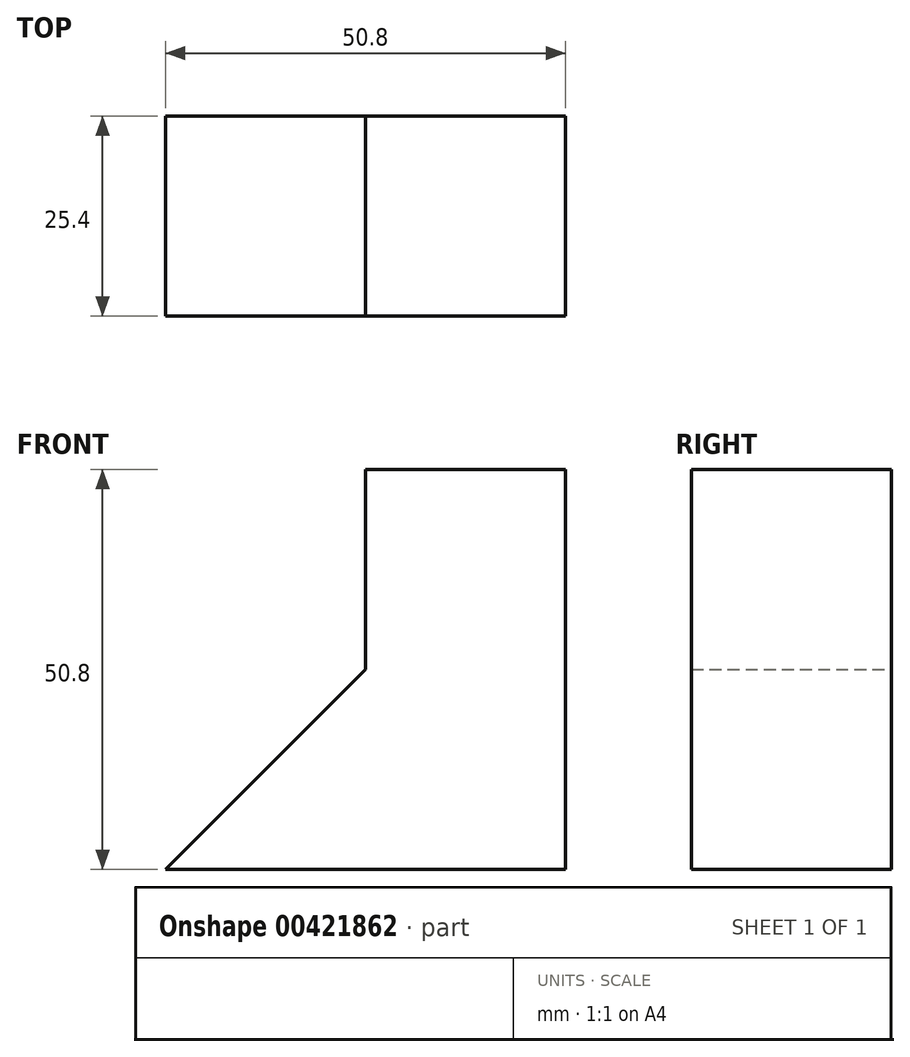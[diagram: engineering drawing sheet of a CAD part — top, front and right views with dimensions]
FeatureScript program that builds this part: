
annotation { "Feature Type Name" : "Feature", "Feature Type Description" : "" }
export const myFeature = defineFeature(function(context is Context, id is Id, definition is map)
    precondition{}
    {
        {
            var Q0;
            Q0=qCreatedBy(makeId("Front.planeOp"),FACE);
            var sketch = newSketch(context, id + "F0", { "sketchPlane" : qUnion([Q0])});
            skLineSegment(sketch, "E0", {"start": v(38.54, 49.98) * mm, "end": v(63.94, 49.98) * mm});
            skLineSegment(sketch, "E1", {"start": v(63.94, 49.98) * mm, "end": v(63.94, -0.82) * mm});
            skLineSegment(sketch, "E2", {"start": v(63.94, -0.82) * mm, "end": v(13.14, -0.82) * mm});
            skLineSegment(sketch, "E3", {"start": v(38.54, 49.98) * mm, "end": v(38.54, 24.58) * mm});
            skLineSegment(sketch, "E4", {"start": v(38.54, 24.58) * mm, "end": v(13.14, -0.82) * mm});
            skSolve(sketch);
        }
        {
            var Q0;
            Q0=makeQuery(id+"F0.imprint","IMPRINT",FACE,{"disambiguationData":[TD([[makeQuery(id+"F0.imprint","IMPRINT",EDGE,{"derivedFrom":sQuery(id+"F0.wireOp",EDGE,"E0")}),-1.0]])]});
            extrude(context, id + "F1", {"entities" : qUnion([Q0]), "depth" : 25.4 * mm});
        }
    });
